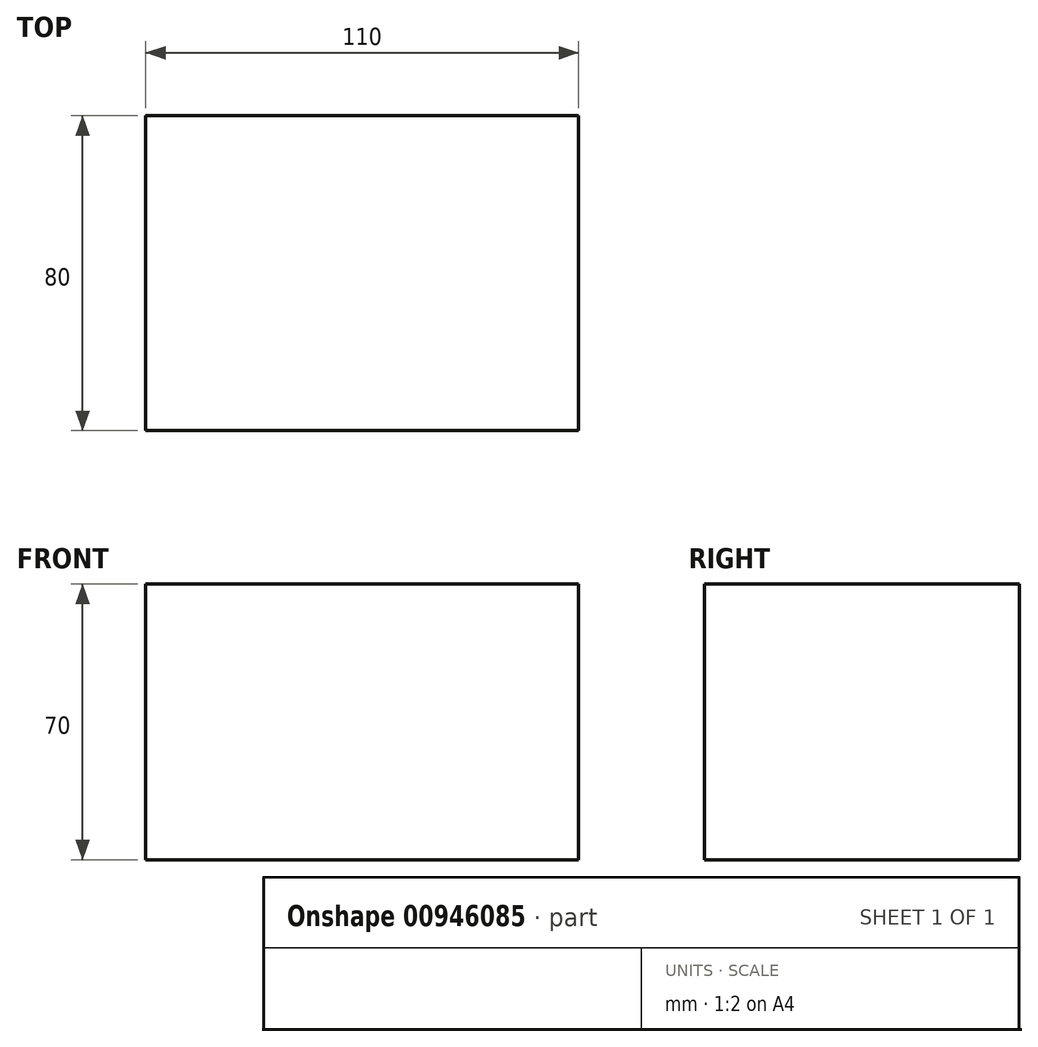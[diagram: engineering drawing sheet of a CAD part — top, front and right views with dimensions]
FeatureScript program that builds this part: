
annotation { "Feature Type Name" : "Feature", "Feature Type Description" : "" }
export const myFeature = defineFeature(function(context is Context, id is Id, definition is map)
    precondition{}
    {
        {
            var Q0;
            Q0=qCreatedBy(makeId("Top.planeOp"),FACE);
            var sketch = newSketch(context, id + "F0", { "sketchPlane" : qUnion([Q0])});
            skLineSegment(sketch, "E0.bottom", {"start": v(-84.81, 64.3) * mm, "end": v(25.19, 64.3) * mm});
            skLineSegment(sketch, "E0.top", {"start": v(-84.81, -15.7) * mm, "end": v(25.19, -15.7) * mm});
            skLineSegment(sketch, "E0.left", {"start": v(-84.81, 64.3) * mm, "end": v(-84.81, -15.7) * mm});
            skLineSegment(sketch, "E0.right", {"start": v(25.19, 64.3) * mm, "end": v(25.19, -15.7) * mm});
            skSolve(sketch);
        }
        {
            var Q0;
            Q0 = qSketchRegion(id + "F0", true);
            extrude(context, id + "F1", {"entities" : qUnion([Q0]), "depth" : 70 * mm, "offsetDistance" : 25 * mm});
        }
    });
